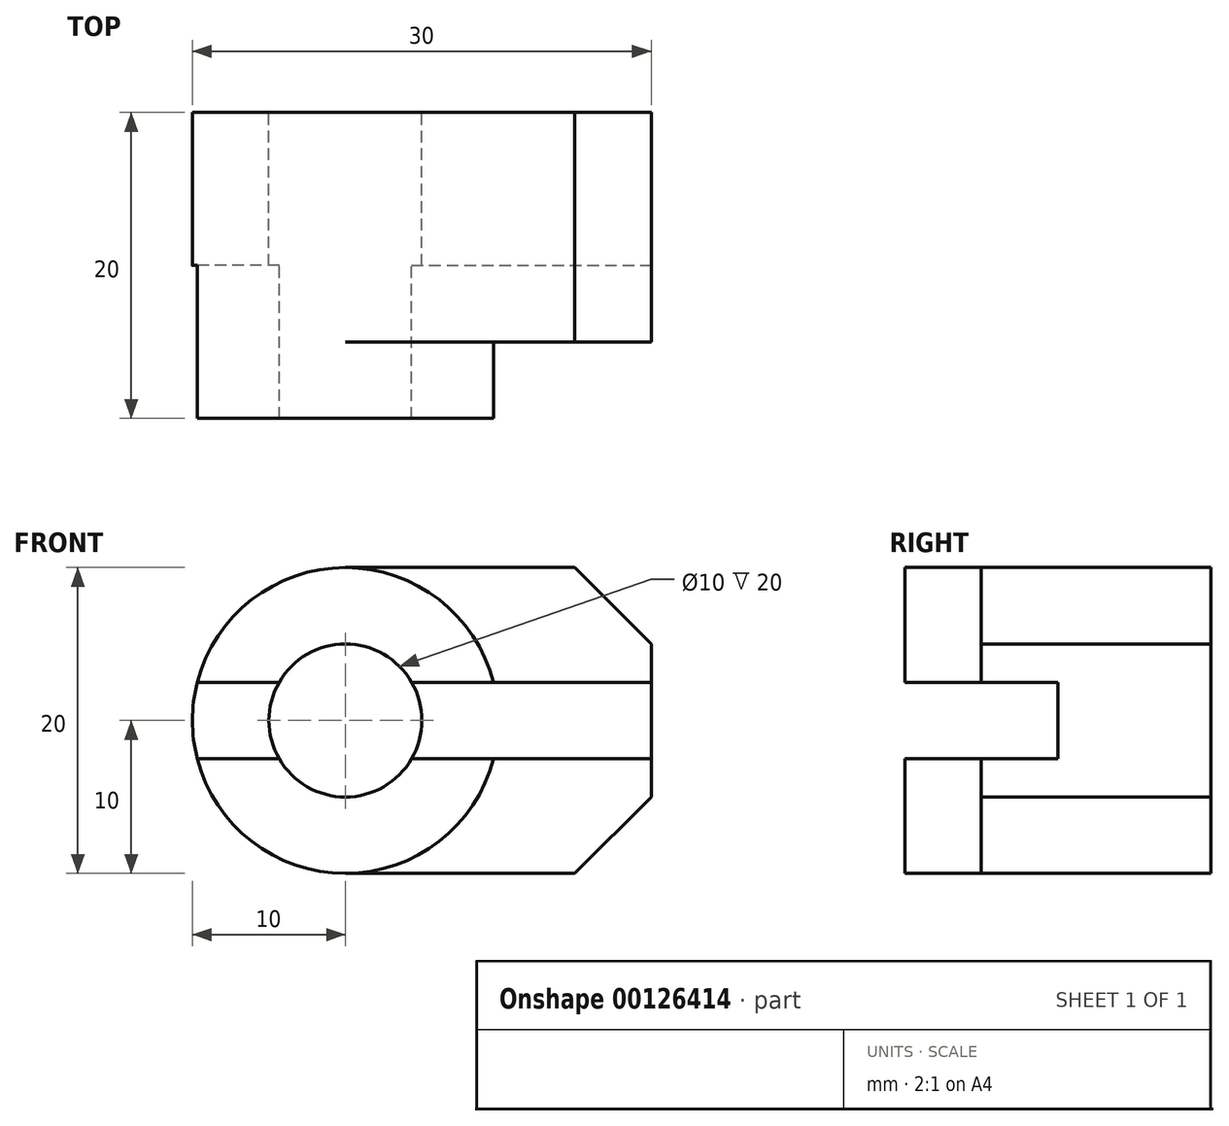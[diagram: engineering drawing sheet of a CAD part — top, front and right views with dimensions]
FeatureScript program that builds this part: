
annotation { "Feature Type Name" : "Feature", "Feature Type Description" : "" }
export const myFeature = defineFeature(function(context is Context, id is Id, definition is map)
    precondition{}
    {
        {
            var Q0;
            Q0=qCreatedBy(makeId("Front.planeOp"),FACE);
            var sketch = newSketch(context, id + "F0", { "sketchPlane" : qUnion([Q0])});
            skCircle(sketch, "E0", {"center": v(0, 0) * mm, "radius": 5 * mm});
            skArc(sketch, "E1", {"start": v(9.68, 2.5) * mm, "mid": v(-10, 0) * mm, "end": v(9.68, -2.5) * mm});
            skLineSegment(sketch, "E2", {"start": v(-16.7, 0) * mm, "end": v(50.26, 0) * mm, "construction": true});
            skLineSegment(sketch, "E3", {"start": v(9.68, 2.5) * mm, "end": v(4.33, 2.5) * mm});
            skLineSegment(sketch, "E4", {"start": v(-9.68, -2.5) * mm, "end": v(-4.33, -2.5) * mm});
            skLineSegment(sketch, "E5.trimOffspring", {"start": v(-4.33, 2.5) * mm, "end": v(-9.68, 2.5) * mm});
            skLineSegment(sketch, "E6.trimOffspring", {"start": v(4.33, -2.5) * mm, "end": v(9.68, -2.5) * mm});
            skLineSegment(sketch, "E7", {"start": v(0, 10) * mm, "end": v(15, 10) * mm});
            skLineSegment(sketch, "E8", {"start": v(20, 5) * mm, "end": v(15, 10) * mm});
            skLineSegment(sketch, "E9", {"start": v(20, 5) * mm, "end": v(20, -5) * mm});
            skLineSegment(sketch, "E10", {"start": v(0, -10) * mm, "end": v(15, -10) * mm});
            skLineSegment(sketch, "E11", {"start": v(20, -5) * mm, "end": v(15, -10) * mm});
            skLineSegment(sketch, "E12", {"start": v(15, -10) * mm, "end": v(15, 10) * mm, "construction": true});
            skLineSegment(sketch, "E13", {"start": v(9.68, 2.5) * mm, "end": v(20, 2.5) * mm});
            skLineSegment(sketch, "E14", {"start": v(9.68, -2.5) * mm, "end": v(20, -2.5) * mm});
            skSolve(sketch);
        }
        {
            var Q0;
            {var subQ3=sQuery(id+"F0.wireOp",EDGE,"E7");Q0=makeQuery(id+"F0.imprint","IMPRINT",FACE,{"disambiguationData":[TD([[makeQuery(id+"F0.imprint","IMPRINT",EDGE,{"derivedFrom":subQ3}),-1.0]])]});}
            var Q1;
            {var subQ4=sQuery(id+"F0.wireOp",EDGE,"E3");Q1=makeQuery(id+"F0.imprint","IMPRINT",FACE,{"disambiguationData":[TD([[makeQuery(id+"F0.imprint","IMPRINT",EDGE,{"derivedFrom":subQ4}),1.0]])]});}
            var Q2;
            {var subQ1=sQuery(id+"F0.wireOp",EDGE,"E10");Q2=makeQuery(id+"F0.imprint","IMPRINT",FACE,{"disambiguationData":[TD([[makeQuery(id+"F0.imprint","IMPRINT",EDGE,{"derivedFrom":subQ1}),1.0]])]});}
            var Q3;
            {var subQ0=sQuery(id+"F0.wireOp",EDGE,"E0");var subQ1=makeQuery(id+"F0.imprint","INTERSECT",VERTEX,{"derivedFrom":[subQ0,sQuery(id+"F0.wireOp",EDGE,"E3")]});Q3=makeQuery(id+"F0.imprint","IMPRINT",FACE,{"disambiguationData":[TD([[makeQuery(id+"F0.imprint","IMPRINT",EDGE,{"disambiguationData":[TD([[subQ1,-1.0]])],"derivedFrom":subQ0}),1.0]])]});}
            var Q4;
            {var subQ0=sQuery(id+"F0.wireOp",EDGE,"E4");Q4=makeQuery(id+"F0.imprint","IMPRINT",FACE,{"disambiguationData":[TD([[makeQuery(id+"F0.imprint","IMPRINT",EDGE,{"derivedFrom":subQ0}),1.0]])]});}
            extrude(context, id + "F1", {"entities" : qUnion([Q0, Q1, Q2, Q3, Q4]), "oppositeDirection" : true, "depth" : 15 * mm});
        }
        {
            var Q0;
            {var subQ0=sQuery(id+"F0.wireOp",EDGE,"E3");Q0=makeQuery(id+"F0.imprint","IMPRINT",FACE,{"disambiguationData":[TD([[makeQuery(id+"F0.imprint","IMPRINT",EDGE,{"derivedFrom":subQ0}),-1.0]])]});}
            var Q1;
            {var subQ0=sQuery(id+"F0.wireOp",EDGE,"E4");Q1=makeQuery(id+"F0.imprint","IMPRINT",FACE,{"disambiguationData":[TD([[makeQuery(id+"F0.imprint","IMPRINT",EDGE,{"derivedFrom":subQ0}),-1.0]])]});}
            extrude(context, id + "F2", {"entities" : qUnion([Q0, Q1]), "operationType" : NewBodyOperationType.ADD, "depth" : 5 * mm, "hasSecondDirection" : true, "secondDirectionOppositeDirection" : true, "secondDirectionDepth" : 15 * mm});
        }
        {
            var Q0;
            {var subQ0=sQuery(id+"F0.wireOp",EDGE,"E0");var subQ1=makeQuery(id+"F0.imprint","INTERSECT",VERTEX,{"derivedFrom":[subQ0,sQuery(id+"F0.wireOp",EDGE,"E3")]});Q0=makeQuery(id+"F0.imprint","IMPRINT",FACE,{"disambiguationData":[TD([[makeQuery(id+"F0.imprint","IMPRINT",EDGE,{"disambiguationData":[TD([[subQ1,-1.0]])],"derivedFrom":subQ0}),1.0]])]});}
            extrude(context, id + "F3", {"entities" : qUnion([Q0]), "operationType" : NewBodyOperationType.REMOVE, "endBound" : BoundingType.THROUGH_ALL, "oppositeDirection" : true, "depth" : 25 * mm});
        }
        {
            var Q0;
            {var subQ4=sQuery(id+"F0.wireOp",EDGE,"E3");Q0=makeQuery(id+"F0.imprint","IMPRINT",FACE,{"disambiguationData":[TD([[makeQuery(id+"F0.imprint","IMPRINT",EDGE,{"derivedFrom":subQ4}),1.0]])]});}
            var Q1;
            {var subQ0=sQuery(id+"F0.wireOp",EDGE,"E4");Q1=makeQuery(id+"F0.imprint","IMPRINT",FACE,{"disambiguationData":[TD([[makeQuery(id+"F0.imprint","IMPRINT",EDGE,{"derivedFrom":subQ0}),1.0]])]});}
            extrude(context, id + "F4", {"entities" : qUnion([Q0, Q1]), "operationType" : NewBodyOperationType.REMOVE, "oppositeDirection" : true, "depth" : 5 * mm});
        }
    });
